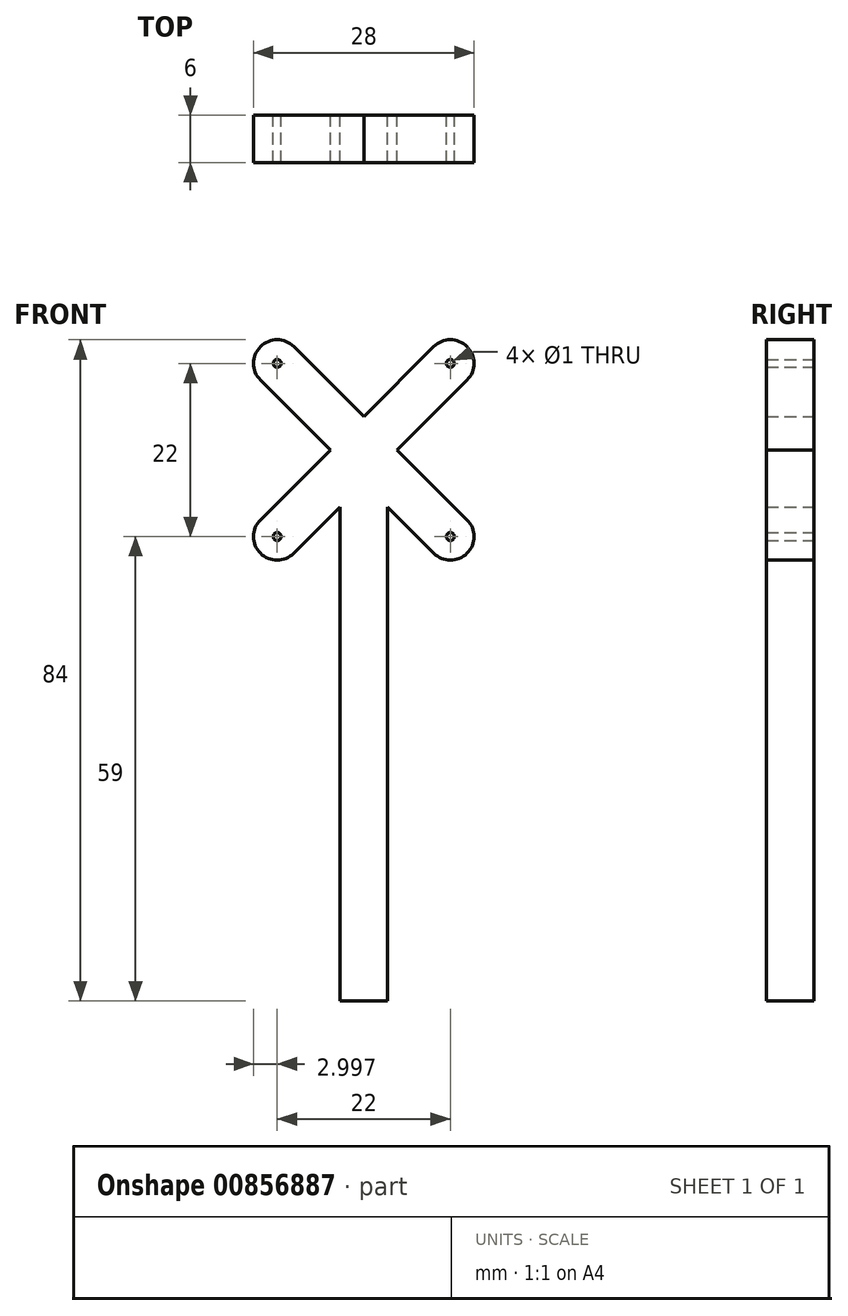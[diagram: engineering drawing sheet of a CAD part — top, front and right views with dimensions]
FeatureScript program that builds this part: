
annotation { "Feature Type Name" : "Feature", "Feature Type Description" : "" }
export const myFeature = defineFeature(function(context is Context, id is Id, definition is map)
    precondition{}
    {
        {
            var Q0;
            Q0=qCreatedBy(makeId("Front.planeOp"),FACE);
            var sketch = newSketch(context, id + "F0", { "sketchPlane" : qUnion([Q0])});
            skLineSegment(sketch, "E0.top", {"start": v(-3, 0) * mm, "end": v(3, 0) * mm});
            skLineSegment(sketch, "E0.right", {"start": v(3, 62.74) * mm, "end": v(3, 0) * mm});
            skLineSegment(sketch, "E1.bottom", {"start": v(-11.01, 81) * mm, "end": v(10.99, 81) * mm, "construction": true});
            skLineSegment(sketch, "E1.top", {"start": v(-11.01, 59) * mm, "end": v(10.99, 59) * mm, "construction": true});
            skLineSegment(sketch, "E1.left", {"start": v(-11.01, 81) * mm, "end": v(-11.01, 59) * mm, "construction": true});
            skLineSegment(sketch, "E1.right", {"start": v(10.99, 81) * mm, "end": v(10.99, 59) * mm, "construction": true});
            skPoint(sketch, "E1.middle", {"position": v(-0.01, 70) * mm});
            skLineSegment(sketch, "E2", {"start": v(-11.01, 81) * mm, "end": v(-10.66, 80.65) * mm, "construction": true});
            skLineSegment(sketch, "E3", {"start": v(10.99, 81) * mm, "end": v(10.63, 80.65) * mm, "construction": true});
            skLineSegment(sketch, "E4.0", {"start": v(-13.13, 78.88) * mm, "end": v(-4.26, 70) * mm});
            skLineSegment(sketch, "E5.0", {"start": v(-8.9, 83.12) * mm, "end": v(-0.01, 74.24) * mm});
            skLineSegment(sketch, "E6.0", {"start": v(8.87, 83.12) * mm, "end": v(-0.01, 74.24) * mm});
            skLineSegment(sketch, "E7.0", {"start": v(13.1, 78.88) * mm, "end": v(4.23, 70) * mm});
            skArc(sketch, "E8", {"start": v(-13.13, 61.12) * mm, "mid": v(-13.13, 56.88) * mm, "end": v(-8.9, 56.88) * mm});
            skArc(sketch, "E9", {"start": v(8.87, 83.12) * mm, "mid": v(13.1, 83.12) * mm, "end": v(13.1, 78.88) * mm});
            skArc(sketch, "E10", {"start": v(13.1, 61.12) * mm, "mid": v(13.1, 56.88) * mm, "end": v(8.87, 56.88) * mm});
            skArc(sketch, "E11", {"start": v(-8.9, 83.12) * mm, "mid": v(-13.13, 83.12) * mm, "end": v(-13.13, 78.88) * mm});
            skCircle(sketch, "E12", {"center": v(-11.01, 81) * mm, "radius": 0.5 * mm});
            skCircle(sketch, "E13", {"center": v(-11.01, 59) * mm, "radius": 0.5 * mm});
            skCircle(sketch, "E14", {"center": v(10.99, 59) * mm, "radius": 0.5 * mm});
            skCircle(sketch, "E15", {"center": v(10.99, 81) * mm, "radius": 0.5 * mm});
            skLineSegment(sketch, "E16.trimOffspring", {"start": v(-4.26, 70) * mm, "end": v(-13.13, 61.12) * mm});
            skLineSegment(sketch, "E17.trimOffspring", {"start": v(4.23, 70) * mm, "end": v(13.1, 61.12) * mm});
            skLineSegment(sketch, "E18.trimOffspring", {"start": v(-3, 62.77) * mm, "end": v(-8.9, 56.88) * mm});
            skLineSegment(sketch, "E19.trimOffspring", {"start": v(3, 62.74) * mm, "end": v(8.87, 56.88) * mm});
            skLineSegment(sketch, "E20.trimOffspring", {"start": v(-3, 62.77) * mm, "end": v(-3, 0) * mm});
            skLineSegment(sketch, "E21.trimOffspring", {"start": v(-10.66, 59.35) * mm, "end": v(-11.01, 59) * mm, "construction": true});
            skLineSegment(sketch, "E22.trimOffspring", {"start": v(10.63, 59.35) * mm, "end": v(10.99, 59) * mm, "construction": true});
            skSolve(sketch);
        }
        {
            var Q0;
            Q0 = qSketchRegion(id + "F0", true);
            var Q1;
            Q1=makeQuery(id+"F0.imprint","IMPRINT",FACE,{"disambiguationData":[TD([[makeQuery(id+"F0.imprint","IMPRINT",EDGE,{"derivedFrom":sQuery(id+"F0.wireOp",EDGE,"E0.top")}),1.0]])]});
            extrude(context, id + "F1", {"entities" : qUnion([Q0, Q1]), "depth" : 6 * mm, "offsetDistance" : 25 * mm});
        }
    });
